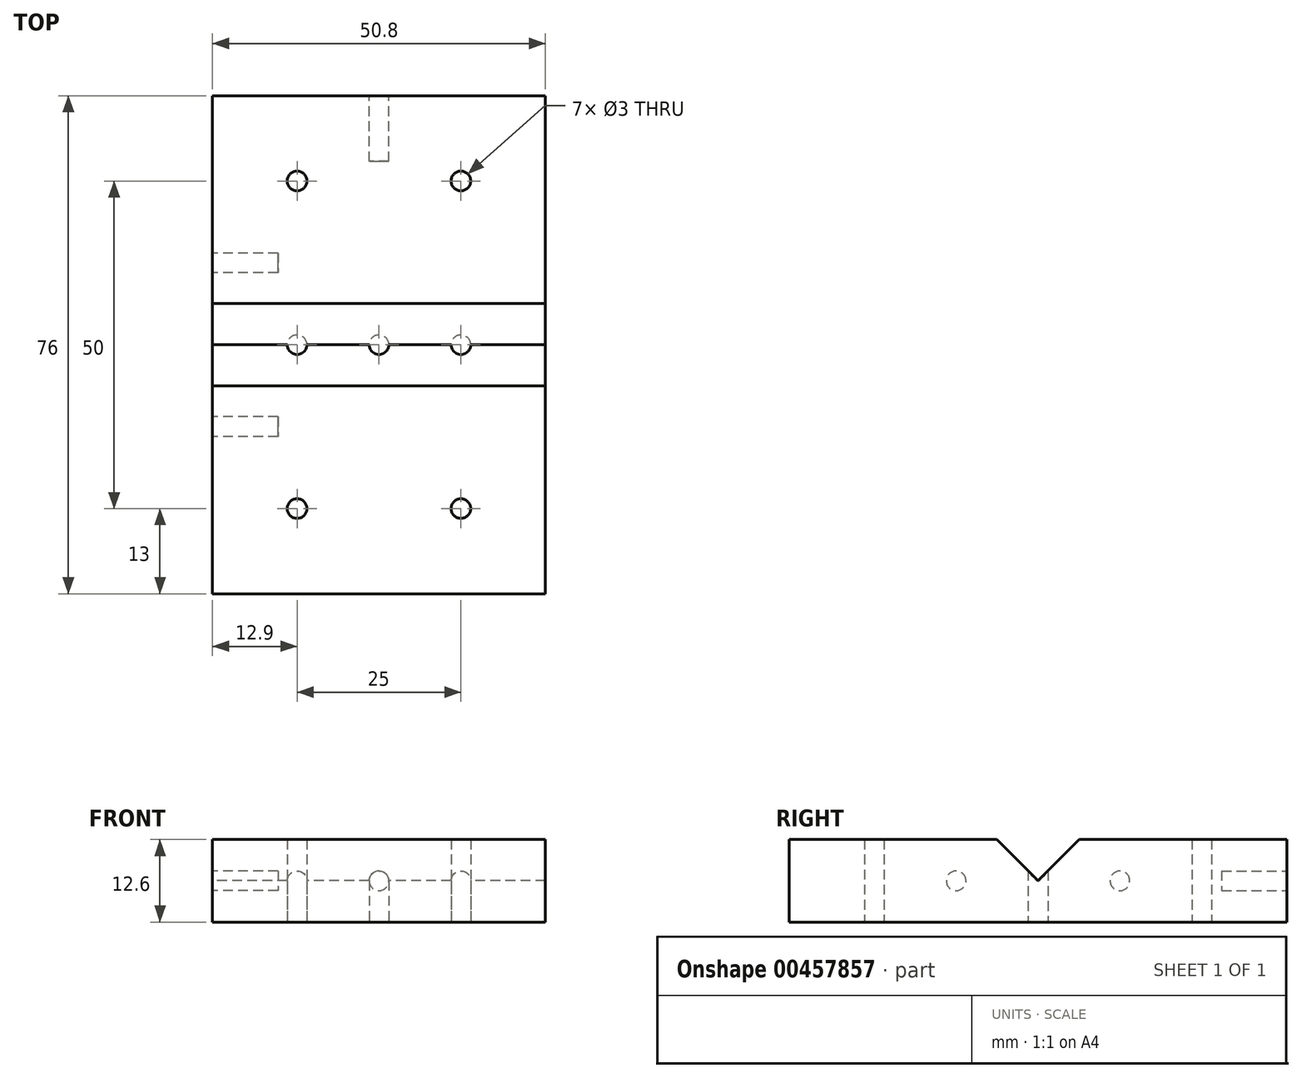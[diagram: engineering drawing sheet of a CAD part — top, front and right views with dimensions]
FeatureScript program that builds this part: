
annotation { "Feature Type Name" : "Feature", "Feature Type Description" : "" }
export const myFeature = defineFeature(function(context is Context, id is Id, definition is map)
    precondition{}
    {
        {
            var Q0;
            Q0=qCreatedBy(makeId("Top.planeOp"),FACE);
            var sketch = newSketch(context, id + "F0", { "sketchPlane" : qUnion([Q0])});
            skLineSegment(sketch, "E0.bottom", {"start": v(25.4, 38) * mm, "end": v(-25.4, 38) * mm});
            skLineSegment(sketch, "E0.top", {"start": v(25.4, -38) * mm, "end": v(-25.4, -38) * mm});
            skLineSegment(sketch, "E0.left", {"start": v(25.4, 38) * mm, "end": v(25.4, -38) * mm});
            skLineSegment(sketch, "E0.right", {"start": v(-25.4, 38) * mm, "end": v(-25.4, -38) * mm});
            skPoint(sketch, "E0.middle", {"position": v(0, 0) * mm});
            skCircle(sketch, "E1", {"center": v(0, 0) * mm, "radius": 1.5 * mm});
            skCircle(sketch, "E2", {"center": v(12.5, 0) * mm, "radius": 1.5 * mm});
            skCircle(sketch, "E3", {"center": v(-12.5, 0) * mm, "radius": 1.5 * mm});
            skCircle(sketch, "E4", {"center": v(-12.5, -25) * mm, "radius": 1.5 * mm});
            skCircle(sketch, "E5", {"center": v(12.5, -25) * mm, "radius": 1.5 * mm});
            skCircle(sketch, "E6", {"center": v(-12.5, 25) * mm, "radius": 1.5 * mm});
            skCircle(sketch, "E7", {"center": v(12.5, 25) * mm, "radius": 1.5 * mm});
            skSolve(sketch);
        }
        {
            var Q0;
            Q0=makeQuery(id+"F0.imprint","IMPRINT",FACE,{"disambiguationData":[TD([[makeQuery(id+"F0.imprint","IMPRINT",EDGE,{"derivedFrom":sQuery(id+"F0.wireOp",EDGE,"E0.bottom")}),1.0]])]});
            extrude(context, id + "F1", {"entities" : qUnion([Q0]), "depth" : 12.6 * mm});
        }
        {
            var Q0;
            Q0=makeQuery(id+"F1.opExtrude","SWEPT_FACE",FACE,{"disambiguationData":[OSD([sQuery(id+"F0.wireOp",EDGE,"E0.right")])]});
            var sketch = newSketch(context, id + "F2", { "sketchPlane" : qUnion([Q0])});
            skLineSegment(sketch, "E8", {"start": v(0, 12.6) * mm, "end": v(6.3, 12.6) * mm});
            skLineSegment(sketch, "E9", {"start": v(6.3, 12.6) * mm, "end": v(0, 6.3) * mm});
            skLineSegment(sketch, "E10", {"start": v(0, 6.3) * mm, "end": v(-6.3, 12.6) * mm});
            skLineSegment(sketch, "E11", {"start": v(-6.3, 12.6) * mm, "end": v(0, 12.6) * mm});
            skCircle(sketch, "E12", {"center": v(-12.5, 6.3) * mm, "radius": 1.5 * mm});
            skPoint(sketch, "E12.centerSnap0", {"position": v(-38, 6.3) * mm});
            skCircle(sketch, "E13", {"center": v(12.5, 6.3) * mm, "radius": 1.5 * mm});
            skSolve(sketch);
        }
        {
            var Q0;
            Q0=makeQuery(id+"F2.imprint","IMPRINT",FACE,{"disambiguationData":[TD([[makeQuery(id+"F2.imprint","IMPRINT",EDGE,{"derivedFrom":sQuery(id+"F2.wireOp",EDGE,"E12")}),1.0]])]});
            var Q1;
            Q1=makeQuery(id+"F2.imprint","IMPRINT",FACE,{"disambiguationData":[TD([[makeQuery(id+"F2.imprint","IMPRINT",EDGE,{"derivedFrom":sQuery(id+"F2.wireOp",EDGE,"E13")}),1.0]])]});
            extrude(context, id + "F3", {"entities" : qUnion([Q0, Q1]), "operationType" : NewBodyOperationType.REMOVE, "oppositeDirection" : true, "depth" : 10 * mm});
        }
        {
            var Q0;
            Q0=makeQuery(id+"F2.imprint","IMPRINT",FACE,{"disambiguationData":[TD([[makeQuery(id+"F2.imprint","IMPRINT",EDGE,{"derivedFrom":sQuery(id+"F2.wireOp",EDGE,"E8")}),-1.0]])]});
            extrude(context, id + "F4", {"entities" : qUnion([Q0]), "operationType" : NewBodyOperationType.REMOVE, "oppositeDirection" : true, "depth" : 50.8 * mm});
        }
        {
            var Q0;
            Q0=makeQuery(id+"F0.imprint","IMPRINT",FACE,{"disambiguationData":[TD([[makeQuery(id+"F0.imprint","IMPRINT",EDGE,{"derivedFrom":sQuery(id+"F0.wireOp",EDGE,"E2")}),1.0]])]});
            var Q1;
            Q1=makeQuery(id+"F0.imprint","IMPRINT",FACE,{"disambiguationData":[TD([[makeQuery(id+"F0.imprint","IMPRINT",EDGE,{"derivedFrom":sQuery(id+"F0.wireOp",EDGE,"E1")}),1.0]])]});
            var Q2;
            Q2=makeQuery(id+"F0.imprint","IMPRINT",FACE,{"disambiguationData":[TD([[makeQuery(id+"F0.imprint","IMPRINT",EDGE,{"derivedFrom":sQuery(id+"F0.wireOp",EDGE,"E3")}),1.0]])]});
            extrude(context, id + "F5", {"entities" : qUnion([Q0, Q1, Q2]), "operationType" : NewBodyOperationType.REMOVE, "depth" : 12 * mm});
        }
        {
            var Q0;
            Q0=makeQuery(id+"F1.opExtrude","SWEPT_FACE",FACE,{"disambiguationData":[OSD([sQuery(id+"F0.wireOp",EDGE,"E0.bottom")])]});
            var sketch = newSketch(context, id + "F6", { "sketchPlane" : qUnion([Q0])});
            skCircle(sketch, "E14", {"center": v(0, 6.3) * mm, "radius": 1.5 * mm});
            skPoint(sketch, "E14.centerSnap0", {"position": v(0, 12.6) * mm});
            skPoint(sketch, "E14.centerSnap1", {"position": v(-25.4, 6.3) * mm});
            skSolve(sketch);
        }
        {
            var Q0;
            Q0=makeQuery(id+"F6.imprint","IMPRINT",FACE,{"disambiguationData":[TD([[makeQuery(id+"F6.imprint","IMPRINT",EDGE,{"derivedFrom":sQuery(id+"F6.wireOp",EDGE,"E14")}),1.0]])]});
            extrude(context, id + "F7", {"entities" : qUnion([Q0]), "operationType" : NewBodyOperationType.REMOVE, "oppositeDirection" : true, "depth" : 10 * mm});
        }
    });
